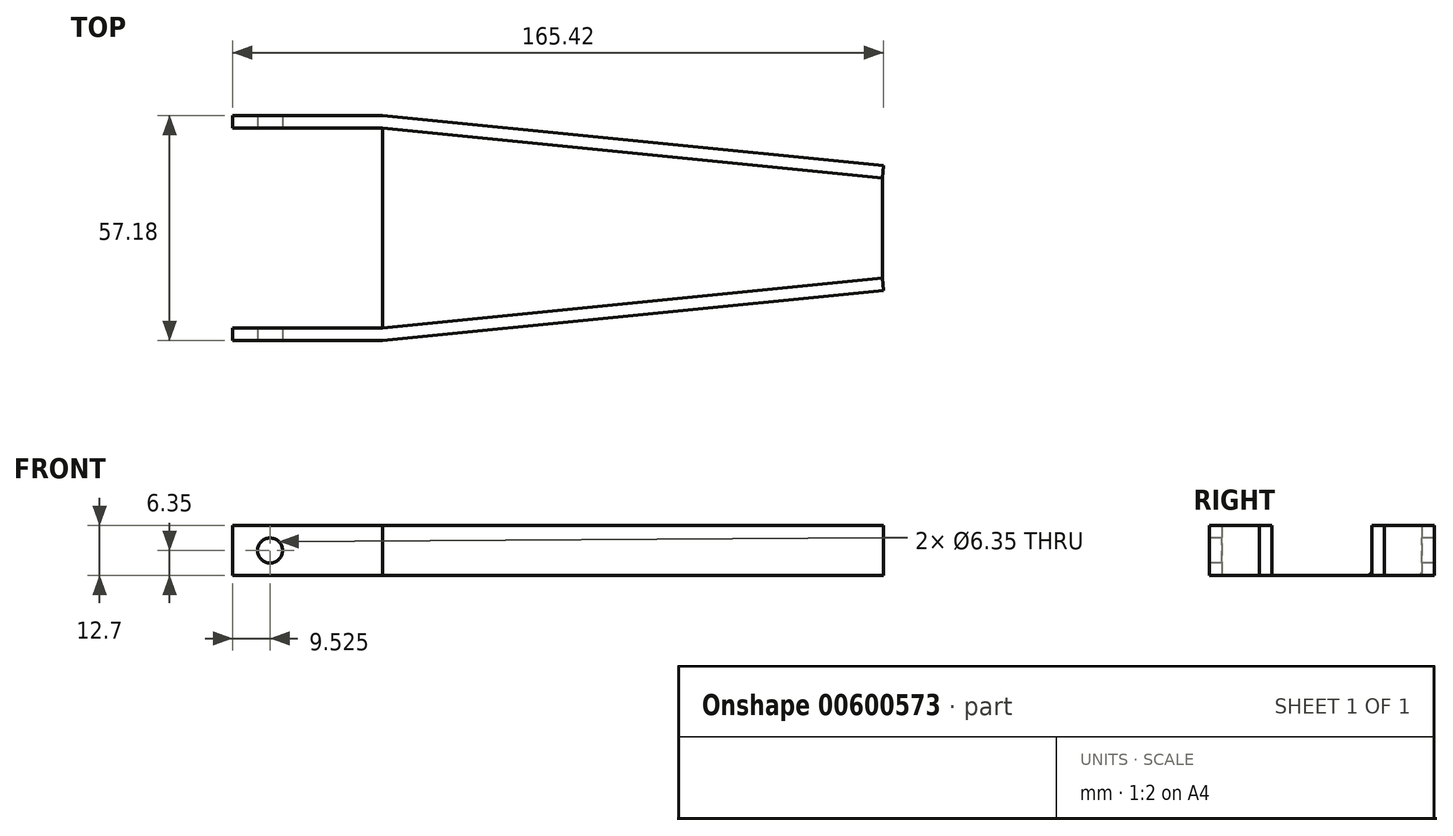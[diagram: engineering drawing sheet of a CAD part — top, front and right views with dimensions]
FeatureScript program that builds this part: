
annotation { "Feature Type Name" : "Feature", "Feature Type Description" : "" }
export const myFeature = defineFeature(function(context is Context, id is Id, definition is map)
    precondition{}
    {
        {
            var Q0;
            Q0=qCreatedBy(makeId("Top.planeOp"),FACE);
            var sketch = newSketch(context, id + "F0", { "sketchPlane" : qUnion([Q0])});
            skLineSegment(sketch, "E0.left", {"start": v(63.5, -12.7) * mm, "end": v(63.5, 12.7) * mm});
            skLineSegment(sketch, "E0.right", {"start": v(-63.5, -25.4) * mm, "end": v(-63.5, 25.4) * mm});
            skPoint(sketch, "E0.middle", {"position": v(0, 0) * mm});
            skLineSegment(sketch, "E1.0", {"start": v(63.5, -12.7) * mm, "end": v(-63.5, -12.7) * mm, "construction": true});
            skLineSegment(sketch, "E2.0", {"start": v(63.5, 12.7) * mm, "end": v(-63.5, 12.7) * mm, "construction": true});
            skLineSegment(sketch, "E3", {"start": v(-63.5, -25.4) * mm, "end": v(63.5, -12.7) * mm});
            skLineSegment(sketch, "E4", {"start": v(-63.5, 25.4) * mm, "end": v(63.5, 12.7) * mm});
            skPoint(sketch, "E5.orphan", {"position": v(63.5, 25.4) * mm});
            skPoint(sketch, "E6.orphan", {"position": v(63.5, -25.4) * mm});
            skSolve(sketch);
        }
        {
            var Q0;
            Q0=makeQuery(id+"F0.imprint","IMPRINT",FACE,{"disambiguationData":[TD([[makeQuery(id+"F0.imprint","IMPRINT",EDGE,{"derivedFrom":sQuery(id+"F0.wireOp",EDGE,"E0.left")}),1.0]])]});
            extrude(context, id + "F1", {"entities" : qUnion([Q0]), "depth" : 1 / 203.2 * mm, "offsetDistance" : 25.4 * mm});
        }
        {
            var Q0;
            Q0=qCreatedBy(makeId("Top.planeOp"),FACE);
            var sketch = newSketch(context, id + "F2", { "sketchPlane" : qUnion([Q0])});
            skLineSegment(sketch, "E7.0", {"start": v(-63.5, -28.6) * mm, "end": v(63.82, -15.86) * mm});
            skLineSegment(sketch, "E8.0", {"start": v(-63.5, -25.4) * mm, "end": v(63.5, -12.7) * mm});
            skLineSegment(sketch, "E9", {"start": v(63.82, -15.86) * mm, "end": v(63.5, -12.7) * mm});
            skLineSegment(sketch, "E10", {"start": v(-63.5, -25.4) * mm, "end": v(-63.5, -28.6) * mm});
            skSolve(sketch);
        }
        {
            var Q0;
            Q0 = qSketchRegion(id + "F2", true);
            extrude(context, id + "F3", {"entities" : qUnion([Q0]), "operationType" : NewBodyOperationType.ADD, "depth" : 12.7 * mm, "offsetDistance" : 25.4 * mm});
        }
        {
            var Q0;
            Q0=makeQuery(id+"F1.opExtrude","SWEPT_BODY",BODY,{"disambiguationData":[OSD([sQuery(id+"F0.wireOp",EDGE,"E0.left"),sQuery(id+"F0.wireOp",EDGE,"E0.right"),sQuery(id+"F0.wireOp",EDGE,"E3"),sQuery(id+"F0.wireOp",EDGE,"E4")])]});
            var Q1;
            Q1=qCreatedBy(makeId("Front.planeOp"),FACE);
            mirror(context, id + "F4", {"operationType" : NewBodyOperationType.ADD, "entities" : qUnion([Q0]), "mirrorPlane" : qUnion([Q1])});
        }
        {
            var Q0;
            Q0=makeQuery(id+"F1.opExtrude","CAP_EDGE",EDGE,{"disambiguationData":[OSD([sQuery(id+"F0.wireOp",EDGE,"E3")])],"isStart":false});
            var Q1;
            Q1=makeQuery(id+"F4.boolean.opBoolean","MERGE",EDGE,{"derivedFrom":[makeQuery(id+"F1.opExtrude","CAP_EDGE",EDGE,{"disambiguationData":[OSD([sQuery(id+"F0.wireOp",EDGE,"E4")])],"isStart":false}),makeQuery(id+"F4.opPattern","COPY",EDGE,{"derivedFrom":makeQuery(id+"F1.opExtrude","CAP_EDGE",EDGE,{"disambiguationData":[OSD([sQuery(id+"F0.wireOp",EDGE,"E3")])],"isStart":false}),"instanceName":"1"})]});
            fillet(context, id + "F5", {"entities" : qUnion([Q0, Q1]), "radius" : 1.27 * mm, "tangentPropagation" : true, "allowEdgeOverflow" : false});
        }
        {
            var Q0;
            {var subQ0=makeQuery(id+"F3.boolean.opBoolean","MERGE",FACE,{"derivedFrom":[makeQuery(id+"F1.opExtrude","SWEPT_FACE",FACE,{"disambiguationData":[OSD([sQuery(id+"F0.wireOp",EDGE,"E0.right")])]}),makeQuery(id+"F3.opExtrude","SWEPT_FACE",FACE,{"disambiguationData":[OSD([sQuery(id+"F2.wireOp",EDGE,"E10")])]})]});Q0=makeQuery(id+"F4.boolean.opBoolean","MERGE",FACE,{"derivedFrom":[subQ0,makeQuery(id+"F4.opPattern","COPY",FACE,{"derivedFrom":subQ0,"instanceName":"1"})]});}
            var sketch = newSketch(context, id + "F6", { "sketchPlane" : qUnion([Q0])});
            skLineSegment(sketch, "E11.bottom", {"start": v(-28.6, 12.7) * mm, "end": v(-25.4, 12.7) * mm});
            skLineSegment(sketch, "E11.top", {"start": v(-28.6, 0) * mm, "end": v(-25.4, 0) * mm});
            skLineSegment(sketch, "E11.left", {"start": v(-28.6, 12.7) * mm, "end": v(-28.6, 0) * mm});
            skLineSegment(sketch, "E11.right", {"start": v(-25.4, 12.7) * mm, "end": v(-25.4, 0) * mm});
            skLineSegment(sketch, "E12.bottom", {"start": v(25.4, 12.7) * mm, "end": v(28.6, 12.7) * mm});
            skLineSegment(sketch, "E12.top", {"start": v(25.4, 0) * mm, "end": v(28.6, 0) * mm});
            skLineSegment(sketch, "E12.left", {"start": v(25.4, 12.7) * mm, "end": v(25.4, 0) * mm});
            skLineSegment(sketch, "E12.right", {"start": v(28.6, 12.7) * mm, "end": v(28.6, 0) * mm});
            skSolve(sketch);
        }
        {
            var Q0;
            {var subQ1=sQuery(id+"F6.wireOp",EDGE,"E11.bottom");Q0=makeQuery(id+"F6.imprint","IMPRINT",FACE,{"disambiguationData":[TD([[makeQuery(id+"F6.imprint","IMPRINT",EDGE,{"derivedFrom":subQ1}),1.0]])]});}
            var Q1;
            {var subQ7=sQuery(id+"F6.wireOp",EDGE,"E12.bottom");Q1=makeQuery(id+"F6.imprint","IMPRINT",FACE,{"disambiguationData":[TD([[makeQuery(id+"F6.imprint","IMPRINT",EDGE,{"derivedFrom":subQ7}),-1.0]])]});}
            extrude(context, id + "F7", {"entities" : qUnion([Q0, Q1]), "operationType" : NewBodyOperationType.ADD, "depth" : 38.1 * mm, "offsetDistance" : 25.4 * mm});
        }
        {
            var Q0;
            Q0=makeQuery(id+"F7.opExtrude","SWEPT_FACE",FACE,{"disambiguationData":[OSD([sQuery(id+"F6.wireOp",EDGE,"E12.right")])]});
            var sketch = newSketch(context, id + "F8", { "sketchPlane" : qUnion([Q0])});
            skLineSegment(sketch, "E13.bottom", {"start": v(-101.6, 12.7) * mm, "end": v(-63.5, 12.7) * mm});
            skLineSegment(sketch, "E13.top", {"start": v(-101.6, 0) * mm, "end": v(-63.5, 0) * mm});
            skLineSegment(sketch, "E13.left", {"start": v(-101.6, 12.7) * mm, "end": v(-101.6, 0) * mm});
            skLineSegment(sketch, "E13.right", {"start": v(-63.5, 12.7) * mm, "end": v(-63.5, 0) * mm});
            skLineSegment(sketch, "E14.0", {"start": v(-92.08, 12.7) * mm, "end": v(-92.08, 0) * mm});
            skPoint(sketch, "E15", {"position": v(-92.08, 6.35) * mm});
            skCircle(sketch, "E16", {"center": v(-92.08, 6.35) * mm, "radius": 3.18 * mm});
            skSolve(sketch);
        }
        {
            var Q0;
            {var subQ0=sQuery(id+"F8.wireOp",EDGE,"E16");var subQ1=sQuery(id+"F8.wireOp",EDGE,"E14.0");var subQ2=makeQuery(id+"F8.imprint","INTERSECT",VERTEX,{"disambiguationData":[OD(0.0)],"derivedFrom":[subQ1,subQ0]});Q0=makeQuery(id+"F8.imprint","IMPRINT",FACE,{"disambiguationData":[TD([[makeQuery(id+"F8.imprint","IMPRINT",EDGE,{"disambiguationData":[TD([[subQ2,-1.0]])],"derivedFrom":subQ1}),-1.0]])]});}
            var Q1;
            {var subQ0=sQuery(id+"F8.wireOp",EDGE,"E16");var subQ1=sQuery(id+"F8.wireOp",EDGE,"E14.0");var subQ2=makeQuery(id+"F8.imprint","INTERSECT",VERTEX,{"disambiguationData":[OD(0.0)],"derivedFrom":[subQ1,subQ0]});Q1=makeQuery(id+"F8.imprint","IMPRINT",FACE,{"disambiguationData":[TD([[makeQuery(id+"F8.imprint","IMPRINT",EDGE,{"disambiguationData":[TD([[subQ2,-1.0]])],"derivedFrom":subQ1}),1.0]])]});}
            extrude(context, id + "F9", {"entities" : qUnion([Q0, Q1]), "operationType" : NewBodyOperationType.REMOVE, "endBound" : BoundingType.THROUGH_ALL, "oppositeDirection" : true, "depth" : 25.4 * mm, "offsetDistance" : 25.4 * mm});
        }
    });
